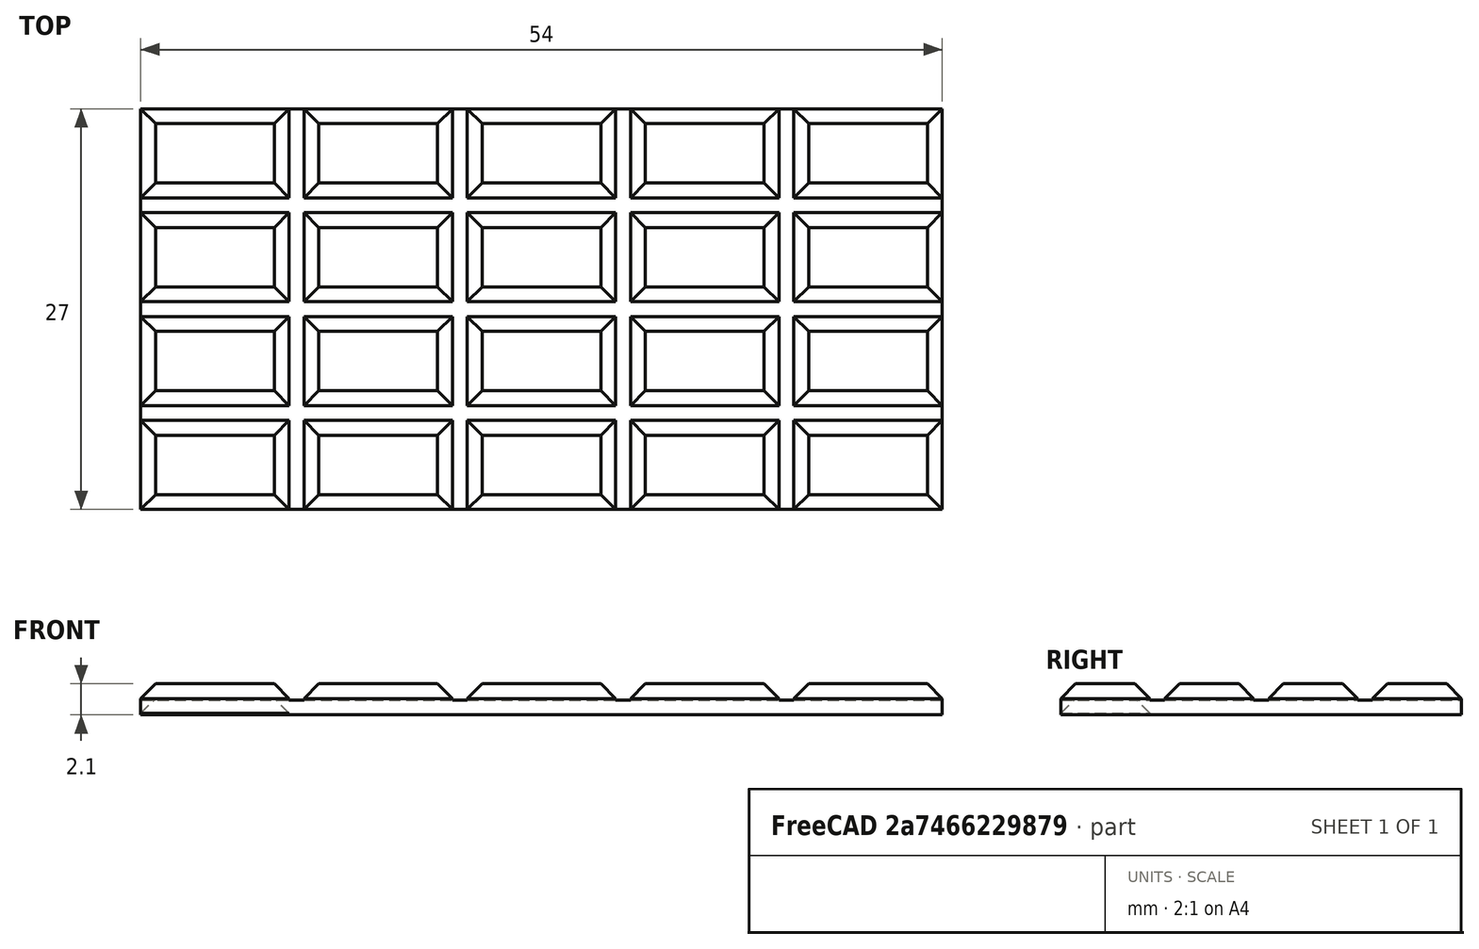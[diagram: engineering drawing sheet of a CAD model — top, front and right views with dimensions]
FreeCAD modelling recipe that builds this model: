
FCSTD DOCUMENT  (FreeCAD 1.0R39319 (Git))
Label: ojt1_t12r02_chocolat
License: All rights reserved
LicenseURL: https://en.wikipedia.org/wiki/All_rights_reserved
objects: Part::Box×2, Part::Chamfer×1, Part::FeaturePython×1, Part::MultiFuse×1
note: 4 computed .brp shape members not serialized (recipe doc carries the construction recipe); baked Part::Feature solids carry a one-line shape summary decoded from their .brp

FEATURE [Part::Box] Box  label="Cub"
  AttacherType = Attacher::AttachEngine3D
  Height = 1.1
  Length = 10
  Width = 6
FEATURE [Part::Chamfer] Chamfer
  Base = -> Box
  EdgeLinks = -> Box [Edge2,Edge6,Edge10,Edge12]
  Edges = 4 edges r=1: [Edge2,Edge6,Edge10,Edge12]
FEATURE [Part::FeaturePython] Array  # Draft array (typed FeaturePython)
  AlwaysSyncPlacement = false
  Angle = 360
  ArrayType = 0
  Axis = (0,0,1)
  Base = -> Chamfer
  Center = (0,0,0)
  Count = 20
  ExpandArray = false
  Fuse = false
  IntervalAxis = (0,0,0)
  IntervalX = (11,0,0)
  IntervalY = (0,7,0)
  IntervalZ = (0,0,100)
  NumberCircles = 3
  NumberPolar = 5
  NumberX = 5
  NumberY = 4
  NumberZ = 1
  Placement = pos=(0,0,1) rot=(0,0,1;0rad)
  PlacementList = 20 placements: [(0,0,0),(0,7,0),(0,14,0),(0,21,0),(11,0,0),(11,7,0),(11,14,0),(11,21,0),(22,0,0),(22,7,0),(22,14,0),(22,21,0),(33,0,0),(33,7,0),(33,14,0),(33,21,0),(44,0,0),(44,7,0),(44,14,0),(44,21,0)]
  RadialDistance = 50
  ScaleList = (20) [(1,1,1),(1,1,1),(1,1,1),(1,1,1),(1,1,1),(1,1,1),(1,1,1),(1,1,1),(1,1,1),(1,1,1),(1,1,1),(1,1,1),(1,1,1),(1,1,1),(1,1,1),(1,1,1),(1,1,1),(1,1,1),(1,1,1),(1,1,1)]
  Symmetry = 1
  TangentialDistance = 25
FEATURE [Part::Box] Box001  label="cub base"
  AttacherType = Attacher::AttachEngine3D
  Height = 1
  Length = 54
  Width = 27
FEATURE [Part::MultiFuse] Fusion
  Shapes = -> [Array,Box001]
